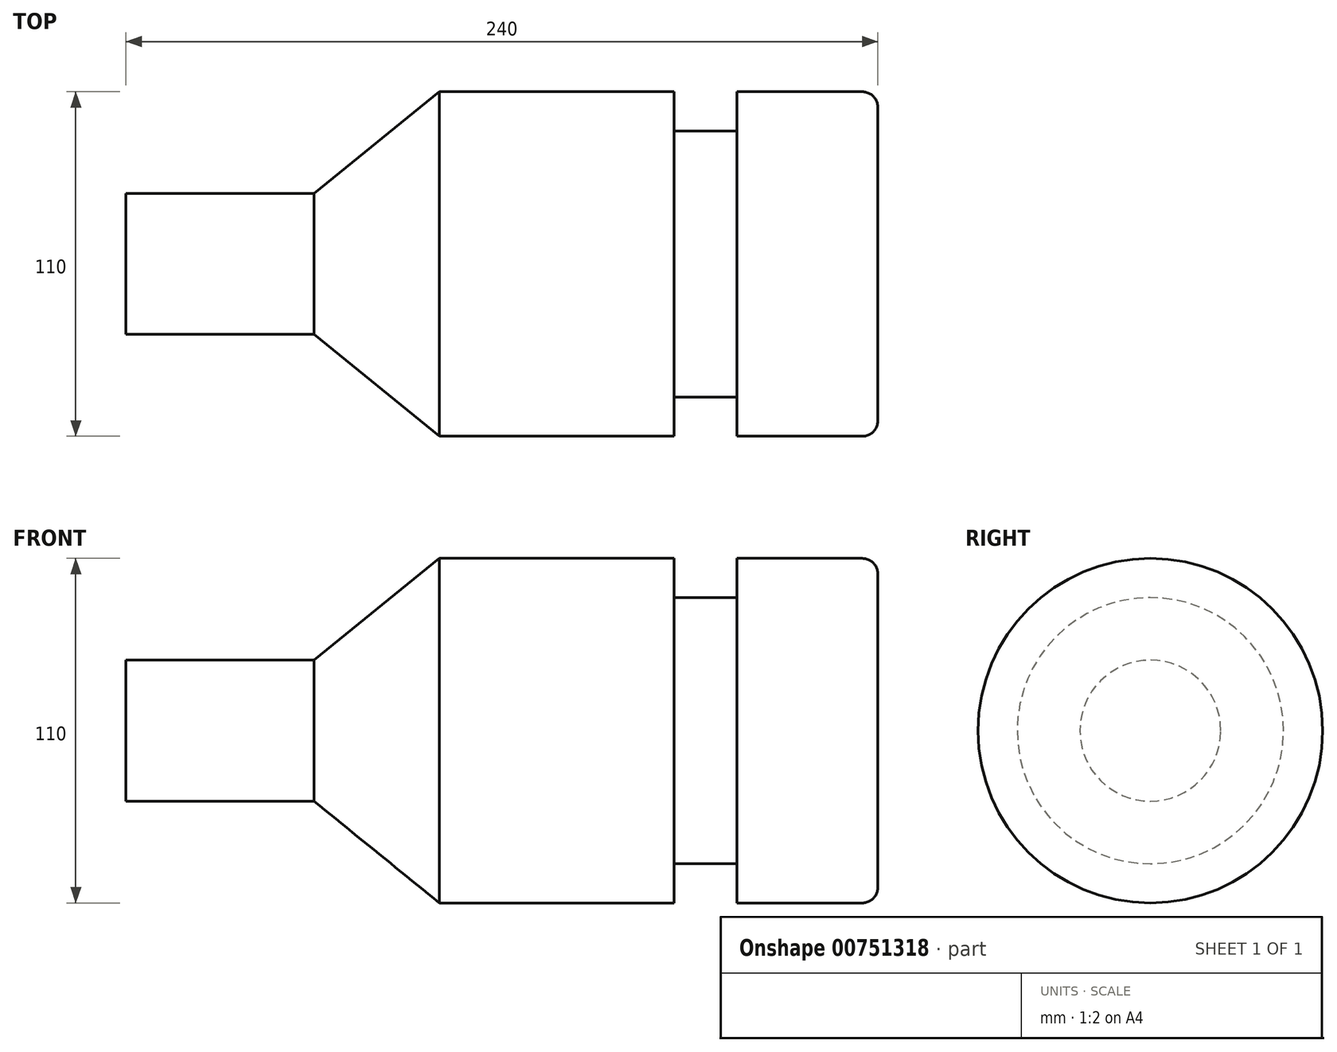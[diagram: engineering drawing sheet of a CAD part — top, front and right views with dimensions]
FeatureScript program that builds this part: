
annotation { "Feature Type Name" : "Feature", "Feature Type Description" : "" }
export const myFeature = defineFeature(function(context is Context, id is Id, definition is map)
    precondition{}
    {
        {
            var Q0;
            Q0=qCreatedBy(makeId("Front.planeOp"),FACE);
            var sketch = newSketch(context, id + "F0", { "sketchPlane" : qUnion([Q0])});
            skLineSegment(sketch, "E0", {"start": v(0, 0) * mm, "end": v(0, 22.5) * mm});
            skLineSegment(sketch, "E1", {"start": v(0, 22.5) * mm, "end": v(60, 22.5) * mm});
            skLineSegment(sketch, "E2", {"start": v(60, 22.5) * mm, "end": v(100, 55) * mm});
            skLineSegment(sketch, "E3", {"start": v(100, 55) * mm, "end": v(175, 55) * mm});
            skLineSegment(sketch, "E4", {"start": v(175, 55) * mm, "end": v(175, 42.5) * mm});
            skLineSegment(sketch, "E5", {"start": v(175, 42.5) * mm, "end": v(195, 42.5) * mm});
            skLineSegment(sketch, "E6", {"start": v(195, 42.5) * mm, "end": v(195, 55) * mm});
            skLineSegment(sketch, "E7", {"start": v(195, 55) * mm, "end": v(235, 55) * mm});
            skLineSegment(sketch, "E8", {"start": v(240, 50) * mm, "end": v(240, 0) * mm});
            skLineSegment(sketch, "E9", {"start": v(240, 0) * mm, "end": v(0, 0) * mm});
            skLineSegment(sketch, "E10", {"start": v(0, 0) * mm, "end": v(-40.23, 0) * mm, "construction": true});
            skPoint(sketch, "E11.visualSharp", {"position": v(240, 55) * mm});
            skArc(sketch, "E11.filletArc", {"start": v(240, 50) * mm, "mid": v(238.54, 53.54) * mm, "end": v(235, 55) * mm});
            skSolve(sketch);
        }
        {
            var Q0;
            Q0=makeQuery(id+"F0.imprint","IMPRINT",FACE,{"disambiguationData":[TD([[makeQuery(id+"F0.imprint","IMPRINT",EDGE,{"derivedFrom":sQuery(id+"F0.wireOp",EDGE,"E0")}),-1.0]])]});
            var Q1;
            Q1=sQuery(id+"F0.wireOp",EDGE,"E10");
            revolve(context, id + "F1", {"surfaceOperationType" : NewSurfaceOperationType.NEW, "entities" : qUnion([Q0]), "axis" : qUnion([Q1]), "revolveType" : RevolveType.FULL});
        }
    });
